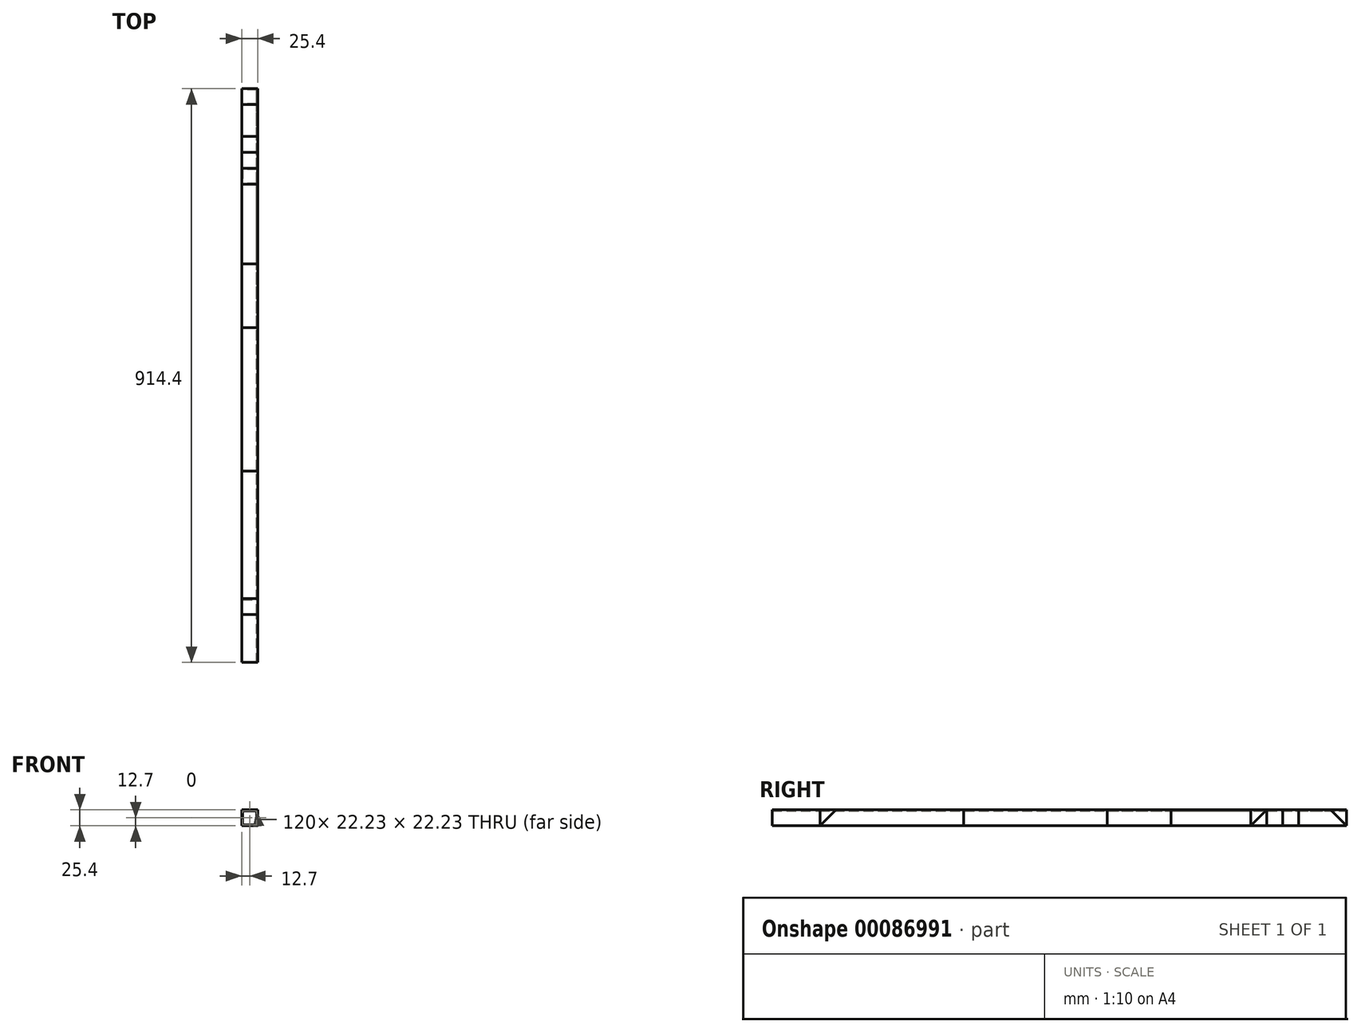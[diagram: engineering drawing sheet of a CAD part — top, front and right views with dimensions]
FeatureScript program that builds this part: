
annotation { "Feature Type Name" : "Feature", "Feature Type Description" : "" }
export const myFeature = defineFeature(function(context is Context, id is Id, definition is map)
    precondition{}
    {
        {
            var Q0;
            Q0=qCreatedBy(makeId("Front.planeOp"),FACE);
            var sketch = newSketch(context, id + "F0", { "sketchPlane" : qUnion([Q0])});
            skLineSegment(sketch, "E0.bottom", {"start": v(0, 0) * mm, "end": v(25.4, 0) * mm});
            skLineSegment(sketch, "E0.top", {"start": v(0, 25.4) * mm, "end": v(25.4, 25.4) * mm});
            skLineSegment(sketch, "E0.left", {"start": v(0, 0) * mm, "end": v(0, 25.4) * mm});
            skLineSegment(sketch, "E0.right", {"start": v(25.4, 0) * mm, "end": v(25.4, 25.4) * mm});
            skLineSegment(sketch, "E1.bottom", {"start": v(1.59, 1.59) * mm, "end": v(23.81, 1.59) * mm});
            skLineSegment(sketch, "E1.top", {"start": v(1.59, 23.81) * mm, "end": v(23.81, 23.81) * mm});
            skLineSegment(sketch, "E1.left", {"start": v(1.59, 1.59) * mm, "end": v(1.59, 23.81) * mm});
            skLineSegment(sketch, "E1.right", {"start": v(23.81, 1.59) * mm, "end": v(23.81, 23.81) * mm});
            skSolve(sketch);
        }
        {
            var Q0;
            Q0=makeQuery(id+"F0.imprint","IMPRINT",FACE,{"disambiguationData":[TD([[makeQuery(id+"F0.imprint","IMPRINT",EDGE,{"derivedFrom":sQuery(id+"F0.wireOp",EDGE,"E0.bottom")}),1.0]])]});
            extrude(context, id + "F1", {"entities" : qUnion([Q0]), "depth" : 914.4 * mm});
        }
        {
            var Q0;
            Q0=qSketchRegion(id+"F0",true);
            extrude(context, id + "F2", {"entities" : qUnion([Q0]), "depth" : 279.4 * mm});
        }
        {
            var Q0;
            Q0=qSketchRegion(id+"F0",true);
            extrude(context, id + "F3", {"entities" : qUnion([Q0]), "depth" : 381 * mm});
        }
        {
            var Q0;
            Q0=qSketchRegion(id+"F0",true);
            extrude(context, id + "F4", {"entities" : qUnion([Q0]), "depth" : 381 * mm});
        }
        {
            var Q0;
            Q0=qSketchRegion(id+"F0",true);
            extrude(context, id + "F5", {"entities" : qUnion([Q0]), "depth" : 609.6 * mm});
        }
        {
            var Q0;
            Q0=qSketchRegion(id+"F0",true);
            extrude(context, id + "F6", {"entities" : qUnion([Q0]), "depth" : 838.2 * mm});
        }
        {
            var Q0;
            Q0=qSketchRegion(id+"F0",true);
            extrude(context, id + "F7", {"entities" : qUnion([Q0]), "depth" : 76.2 * mm});
        }
        {
            var Q0;
            Q0=qSketchRegion(id+"F0",true);
            extrude(context, id + "F8", {"entities" : qUnion([Q0]), "depth" : 838.2 * mm});
        }
        {
            var Q0;
            Q0=qSketchRegion(id+"F0",true);
            extrude(context, id + "F9", {"entities" : qUnion([Q0]), "depth" : 152.4 * mm});
        }
        {
            var Q0;
            Q0=makeQuery(id+"F9.opExtrude","SWEPT_FACE",FACE,{"disambiguationData":[OSD([sQuery(id+"F0.wireOp",EDGE,"E0.right")])]});
            var sketch = newSketch(context, id + "F10", { "sketchPlane" : qUnion([Q0])});
            skLineSegment(sketch, "E2", {"start": v(-152.4, 0) * mm, "end": v(-127, 25.4) * mm});
            skLineSegment(sketch, "E3", {"start": v(0, 0) * mm, "end": v(-25.4, 25.4) * mm});
            skLineSegment(sketch, "E4", {"start": v(-127, 25.4) * mm, "end": v(-152.4, 25.4) * mm});
            skLineSegment(sketch, "E5", {"start": v(-152.4, 0) * mm, "end": v(-152.4, 25.4) * mm});
            skLineSegment(sketch, "E6", {"start": v(-25.4, 25.4) * mm, "end": v(0, 25.4) * mm});
            skSolve(sketch);
        }
        {
            var Q0;
            Q0=makeQuery(id+"F10.imprint","IMPRINT",FACE,{"disambiguationData":[TD([[makeQuery(id+"F10.imprint","IMPRINT",EDGE,{"derivedFrom":sQuery(id+"F10.wireOp",EDGE,"E2")}),1.0]])]});
            var Q1;
            Q1=makeQuery(id+"F10.imprint","IMPRINT",FACE,{"disambiguationData":[TD([[makeQuery(id+"F10.imprint","IMPRINT",EDGE,{"derivedFrom":sQuery(id+"F10.wireOp",EDGE,"E3")}),-1.0]])]});
            extrude(context, id + "F11", {"entities" : qUnion([Q0, Q1]), "operationType" : NewBodyOperationType.REMOVE, "oppositeDirection" : true, "depth" : 25.4 * mm});
        }
        {
            var Q0;
            Q0=makeQuery(id+"F6.opExtrude","SWEPT_FACE",FACE,{"disambiguationData":[OSD([sQuery(id+"F0.wireOp",EDGE,"E0.right")])]});
            var sketch = newSketch(context, id + "F12", { "sketchPlane" : qUnion([Q0])});
            skLineSegment(sketch, "E7", {"start": v(-838.2, 0) * mm, "end": v(-838.2, 25.4) * mm});
            skLineSegment(sketch, "E8", {"start": v(-838.2, 25.4) * mm, "end": v(-812.8, 25.4) * mm});
            skLineSegment(sketch, "E9", {"start": v(-812.8, 25.4) * mm, "end": v(-838.2, 0) * mm});
            skLineSegment(sketch, "E10", {"start": v(0, 0) * mm, "end": v(0, 25.4) * mm});
            skLineSegment(sketch, "E11", {"start": v(0, 25.4) * mm, "end": v(-25.4, 25.4) * mm});
            skLineSegment(sketch, "E12", {"start": v(-25.4, 25.4) * mm, "end": v(0, 0) * mm});
            skSolve(sketch);
        }
        {
            var Q0;
            Q0=makeQuery(id+"F12.imprint","IMPRINT",FACE,{"disambiguationData":[TD([[makeQuery(id+"F12.imprint","IMPRINT",EDGE,{"derivedFrom":sQuery(id+"F12.wireOp",EDGE,"E10")}),1.0]])]});
            var Q1;
            Q1=makeQuery(id+"F12.imprint","IMPRINT",FACE,{"disambiguationData":[TD([[makeQuery(id+"F12.imprint","IMPRINT",EDGE,{"derivedFrom":sQuery(id+"F12.wireOp",EDGE,"E7")}),-1.0]])]});
            extrude(context, id + "F13", {"entities" : qUnion([Q0, Q1]), "operationType" : NewBodyOperationType.REMOVE, "oppositeDirection" : true, "depth" : 25.4 * mm});
        }
        {
            var Q0;
            Q0=qSketchRegion(id+"F0",true);
            extrude(context, id + "F14", {"entities" : qUnion([Q0]), "depth" : 838.2 * mm});
        }
        {
            var Q0;
            Q0 = qSketchRegion(id + "F0", true);
            extrude(context, id + "F15", {"entities" : qUnion([Q0]), "depth" : 101.6 * mm});
        }
        {
            var Q0;
            Q0 = qSketchRegion(id + "F0", true);
            extrude(context, id + "F16", {"entities" : qUnion([Q0]), "depth" : 127 * mm});
        }
    });
